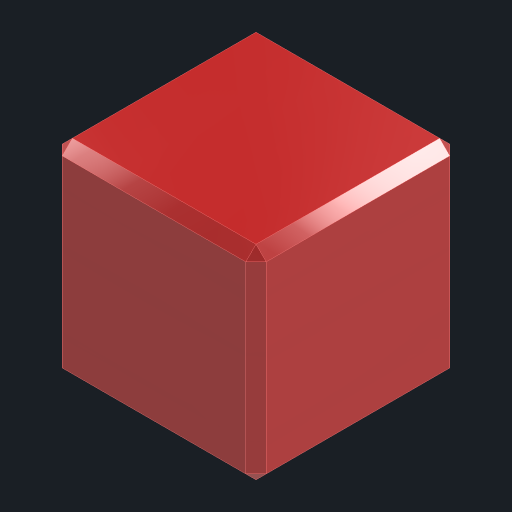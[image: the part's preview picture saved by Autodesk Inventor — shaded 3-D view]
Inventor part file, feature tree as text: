
AUTODESK INVENTOR PART (.ipt)
format: ipt  version: 2023 (Build 270158000, 158)  size: 178,176 bytes
history: native  units: mm
features: extrude x1, chamfer x1, sketch x1
ambient origin geometry x8: Origin, YZ Plane, XZ Plane, XY Plane, X Axis, Y Axis, Z Axis, Center Point
bodies: Solid1 (feature_tree)
feature tree (3):
  extrude  "Extrusion1"  Depth=40.0mm
  chamfer  "Chamfer1"  Distance=40.0mm
  sketch  "Sketch1"  dims[d0=40.0mm d1=40.0mm d2=40.0mm d3=0.0mm d4=2.0mm d5=2.0mm d6=45.0deg]
